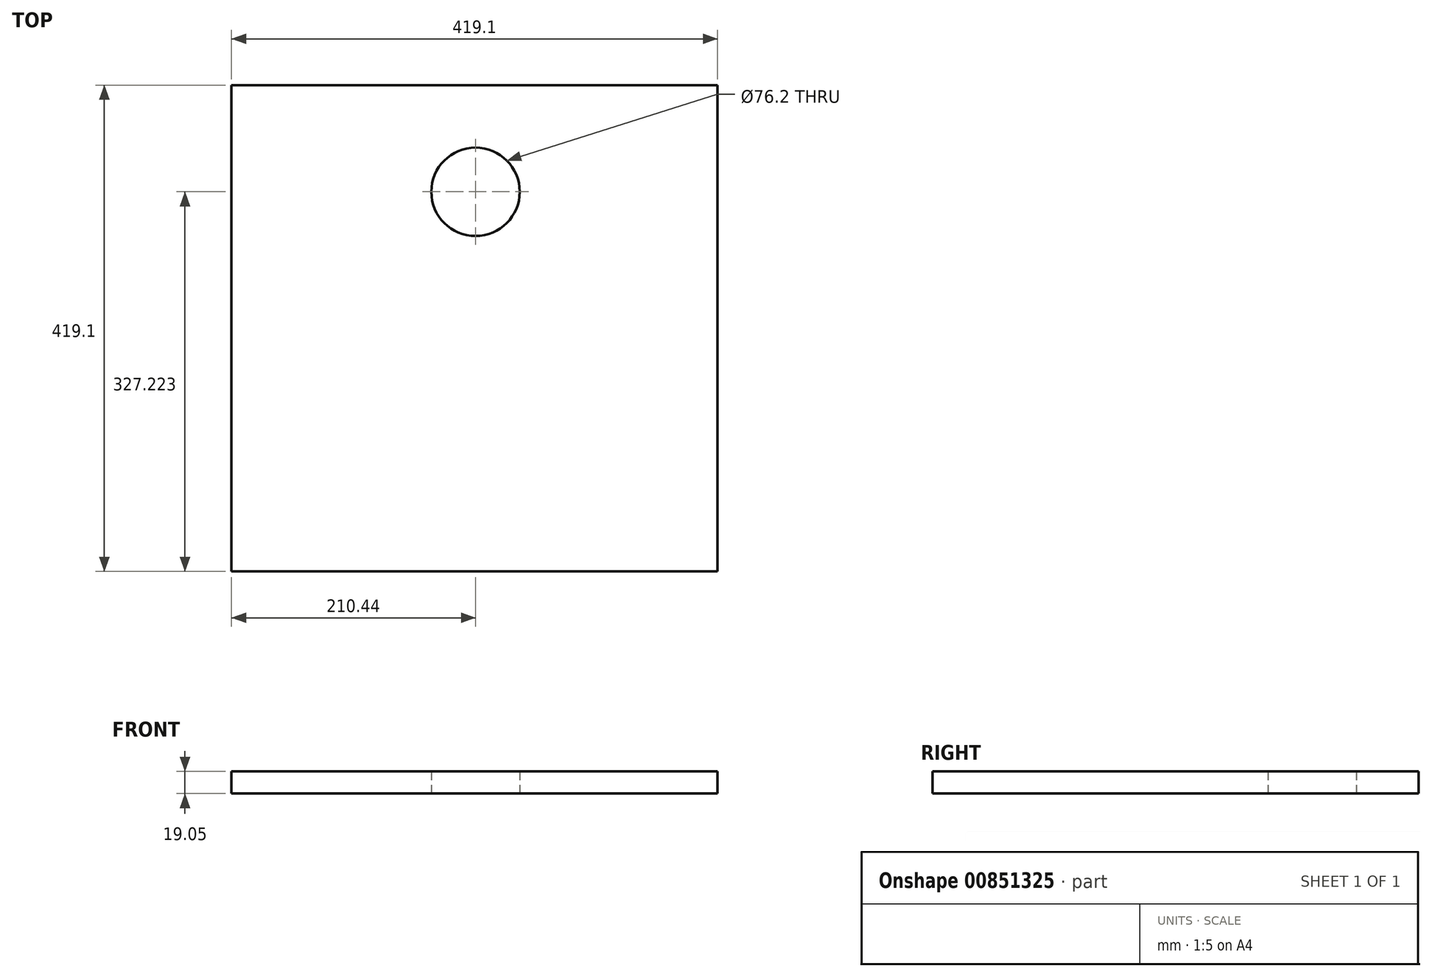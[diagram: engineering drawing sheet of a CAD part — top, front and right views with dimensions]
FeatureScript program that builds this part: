
annotation { "Feature Type Name" : "Feature", "Feature Type Description" : "" }
export const myFeature = defineFeature(function(context is Context, id is Id, definition is map)
    precondition{}
    {
        {
            var Q0;
            Q0=qCreatedBy(makeId("Top.planeOp"),FACE);
            var sketch = newSketch(context, id + "F0", { "sketchPlane" : qUnion([Q0])});
            skLineSegment(sketch, "E0.bottom", {"start": v(-210.44, 138.86) * mm, "end": v(208.66, 138.86) * mm});
            skLineSegment(sketch, "E0.top", {"start": v(-210.44, -280.24) * mm, "end": v(208.66, -280.24) * mm});
            skLineSegment(sketch, "E0.left", {"start": v(-210.44, 138.86) * mm, "end": v(-210.44, -280.24) * mm});
            skLineSegment(sketch, "E0.right", {"start": v(208.66, 138.86) * mm, "end": v(208.66, -280.24) * mm});
            skCircle(sketch, "E1", {"center": v(0, 46.98) * mm, "radius": 38.1 * mm});
            skSolve(sketch);
        }
        {
            var Q0;
            Q0=makeQuery(id+"F0.imprint","IMPRINT",FACE,{"disambiguationData":[TD([[makeQuery(id+"F0.imprint","IMPRINT",EDGE,{"derivedFrom":sQuery(id+"F0.wireOp",EDGE,"E0.bottom")}),-1.0]])]});
            extrude(context, id + "F1", {"entities" : qUnion([Q0]), "depth" : 19.05 * mm, "offsetDistance" : 25.4 * mm});
        }
    });
